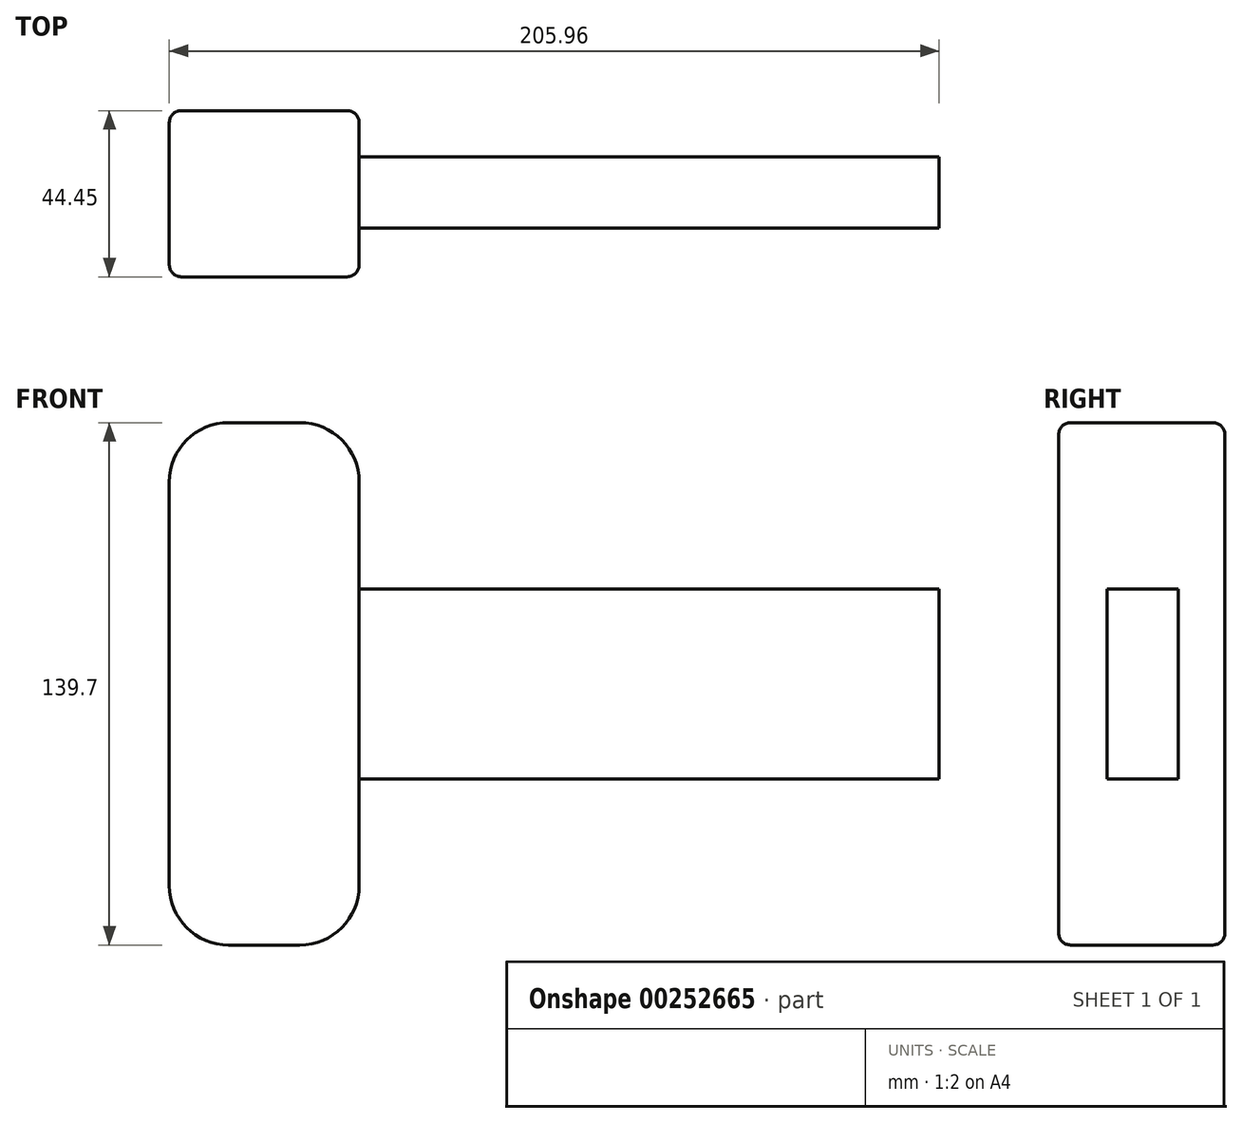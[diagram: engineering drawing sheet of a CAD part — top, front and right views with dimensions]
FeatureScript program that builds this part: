
annotation { "Feature Type Name" : "Feature", "Feature Type Description" : "" }
export const myFeature = defineFeature(function(context is Context, id is Id, definition is map)
    precondition{}
    {
        {
            var Q0;
            Q0=qCreatedBy(makeId("Front.planeOp"),FACE);
            var sketch = newSketch(context, id + "F0", { "sketchPlane" : qUnion([Q0])});
            skLineSegment(sketch, "E0.bottom", {"start": v(-9.52, 69.85) * mm, "end": v(9.53, 69.85) * mm});
            skLineSegment(sketch, "E0.top", {"start": v(-9.53, -69.85) * mm, "end": v(9.53, -69.85) * mm});
            skLineSegment(sketch, "E0.left", {"start": v(-25.4, 53.98) * mm, "end": v(-25.4, -53.98) * mm});
            skLineSegment(sketch, "E0.right", {"start": v(25.4, 53.98) * mm, "end": v(25.4, -53.98) * mm});
            skPoint(sketch, "E0.middle", {"position": v(0, 0) * mm});
            skPoint(sketch, "E1.visualSharp", {"position": v(-25.4, 69.85) * mm});
            skArc(sketch, "E1.filletArc", {"start": v(-9.52, 69.85) * mm, "mid": v(-20.75, 65.2) * mm, "end": v(-25.4, 53.98) * mm});
            skPoint(sketch, "E2.visualSharp", {"position": v(25.4, -69.85) * mm});
            skArc(sketch, "E2.filletArc", {"start": v(9.53, -69.85) * mm, "mid": v(20.75, -65.2) * mm, "end": v(25.4, -53.98) * mm});
            skPoint(sketch, "E3.visualSharp", {"position": v(-25.4, -69.85) * mm});
            skArc(sketch, "E3.filletArc", {"start": v(-25.4, -53.98) * mm, "mid": v(-20.75, -65.2) * mm, "end": v(-9.53, -69.85) * mm});
            skPoint(sketch, "E4.visualSharp", {"position": v(25.4, 69.85) * mm});
            skArc(sketch, "E4.filletArc", {"start": v(25.4, 53.98) * mm, "mid": v(20.75, 65.2) * mm, "end": v(9.53, 69.85) * mm});
            skSolve(sketch);
        }
        {
            var Q0;
            Q0=makeQuery(id+"F0.imprint","IMPRINT",FACE,{"disambiguationData":[TD([[makeQuery(id+"F0.imprint","IMPRINT",EDGE,{"derivedFrom":sQuery(id+"F0.wireOp",EDGE,"E0.bottom")}),-1.0]])]});
            extrude(context, id + "F1", {"entities" : qUnion([Q0]), "depth" : 44.45 * mm});
        }
        {
            var Q0;
            Q0=makeQuery(id+"F1.opExtrude","CAP_EDGE",EDGE,{"disambiguationData":[OSD([sQuery(id+"F0.wireOp",EDGE,"E0.bottom")])],"isStart":false});
            var Q1;
            Q1=makeQuery(id+"F1.opExtrude","CAP_EDGE",EDGE,{"disambiguationData":[OSD([sQuery(id+"F0.wireOp",EDGE,"E4.filletArc")])],"isStart":true});
            fillet(context, id + "F2", {"entities" : qUnion([Q0, Q1]), "radius" : 3.17 * mm, "tangentPropagation" : true, "allowEdgeOverflow" : false});
        }
        {
            var Q0;
            Q0=makeQuery(id+"F1.opExtrude","SWEPT_FACE",FACE,{"disambiguationData":[OSD([sQuery(id+"F0.wireOp",EDGE,"E0.right")])]});
            var sketch = newSketch(context, id + "F3", { "sketchPlane" : qUnion([Q0])});
            skLineSegment(sketch, "E5.bottom", {"start": v(-12.4, -25.4) * mm, "end": v(-31.45, -25.4) * mm});
            skLineSegment(sketch, "E5.top", {"start": v(-12.4, 25.4) * mm, "end": v(-31.45, 25.4) * mm});
            skLineSegment(sketch, "E5.left", {"start": v(-12.4, -25.4) * mm, "end": v(-12.4, 25.4) * mm});
            skLineSegment(sketch, "E5.right", {"start": v(-31.45, -25.4) * mm, "end": v(-31.45, 25.4) * mm});
            skPoint(sketch, "E5.middle", {"position": v(-21.92, 0) * mm});
            skSolve(sketch);
        }
        {
            var Q0;
            Q0=makeQuery(id+"F3.imprint","IMPRINT",FACE,{"disambiguationData":[TD([[makeQuery(id+"F3.imprint","IMPRINT",EDGE,{"derivedFrom":sQuery(id+"F3.wireOp",EDGE,"E5.bottom")}),-1.0]])]});
            extrude(context, id + "F4", {"entities" : qUnion([Q0]), "operationType" : NewBodyOperationType.ADD, "endBound" : BoundingType.THROUGH_ALL, "depth" : 25.4 * mm});
        }
    });
